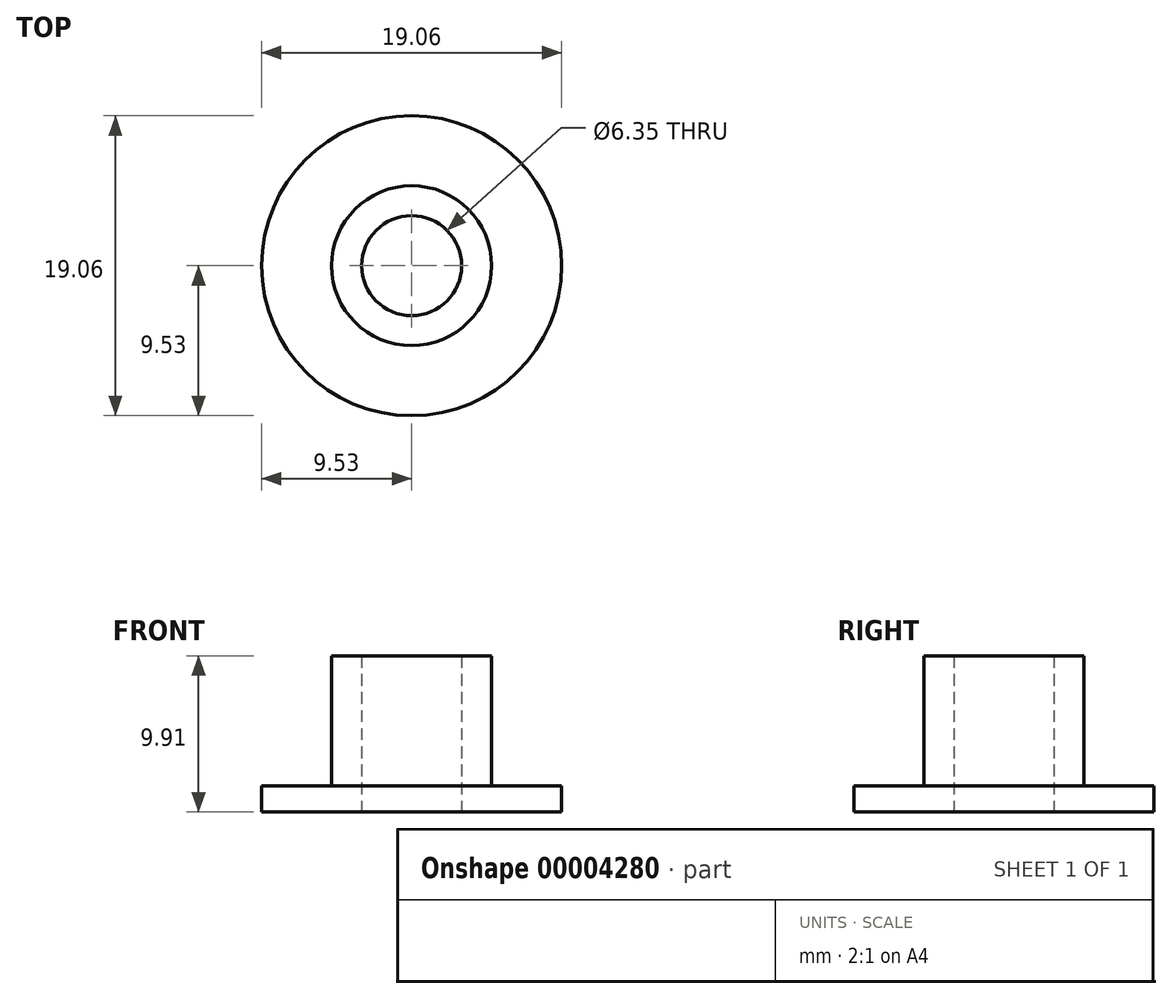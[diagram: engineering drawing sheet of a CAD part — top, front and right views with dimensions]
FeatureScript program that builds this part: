
annotation { "Feature Type Name" : "Feature", "Feature Type Description" : "" }
export const myFeature = defineFeature(function(context is Context, id is Id, definition is map)
    precondition{}
    {
        {
            var Q0;
            Q0=qCreatedBy(makeId("Top.planeOp"),FACE);
            var sketch = newSketch(context, id + "F0", { "sketchPlane" : qUnion([Q0])});
            skCircle(sketch, "E0", {"center": v(0, 0) * mm, "radius": 9.53 * mm});
            skCircle(sketch, "E1", {"center": v(0, 0) * mm, "radius": 3.18 * mm});
            skCircle(sketch, "E2", {"center": v(0, 0) * mm, "radius": 5.08 * mm});
            skSolve(sketch);
        }
        {
            var Q0;
            Q0=makeQuery(id+"F0.imprint","IMPRINT",FACE,{"disambiguationData":[TD([[makeQuery(id+"F0.imprint","IMPRINT",EDGE,{"derivedFrom":sQuery(id+"F0.wireOp",EDGE,"E1")}),-1.0]])]});
            extrude(context, id + "F1", {"entities" : qUnion([Q0]), "depth" : 9.9 * mm, "offsetDistance" : 25.4 * mm});
        }
        {
            var Q0;
            Q0 = qSketchRegion(id + "F0", true);
            extrude(context, id + "F2", {"entities" : qUnion([Q0]), "operationType" : NewBodyOperationType.ADD, "depth" : 1.65 * mm, "offsetDistance" : 25.4 * mm});
        }
    });
